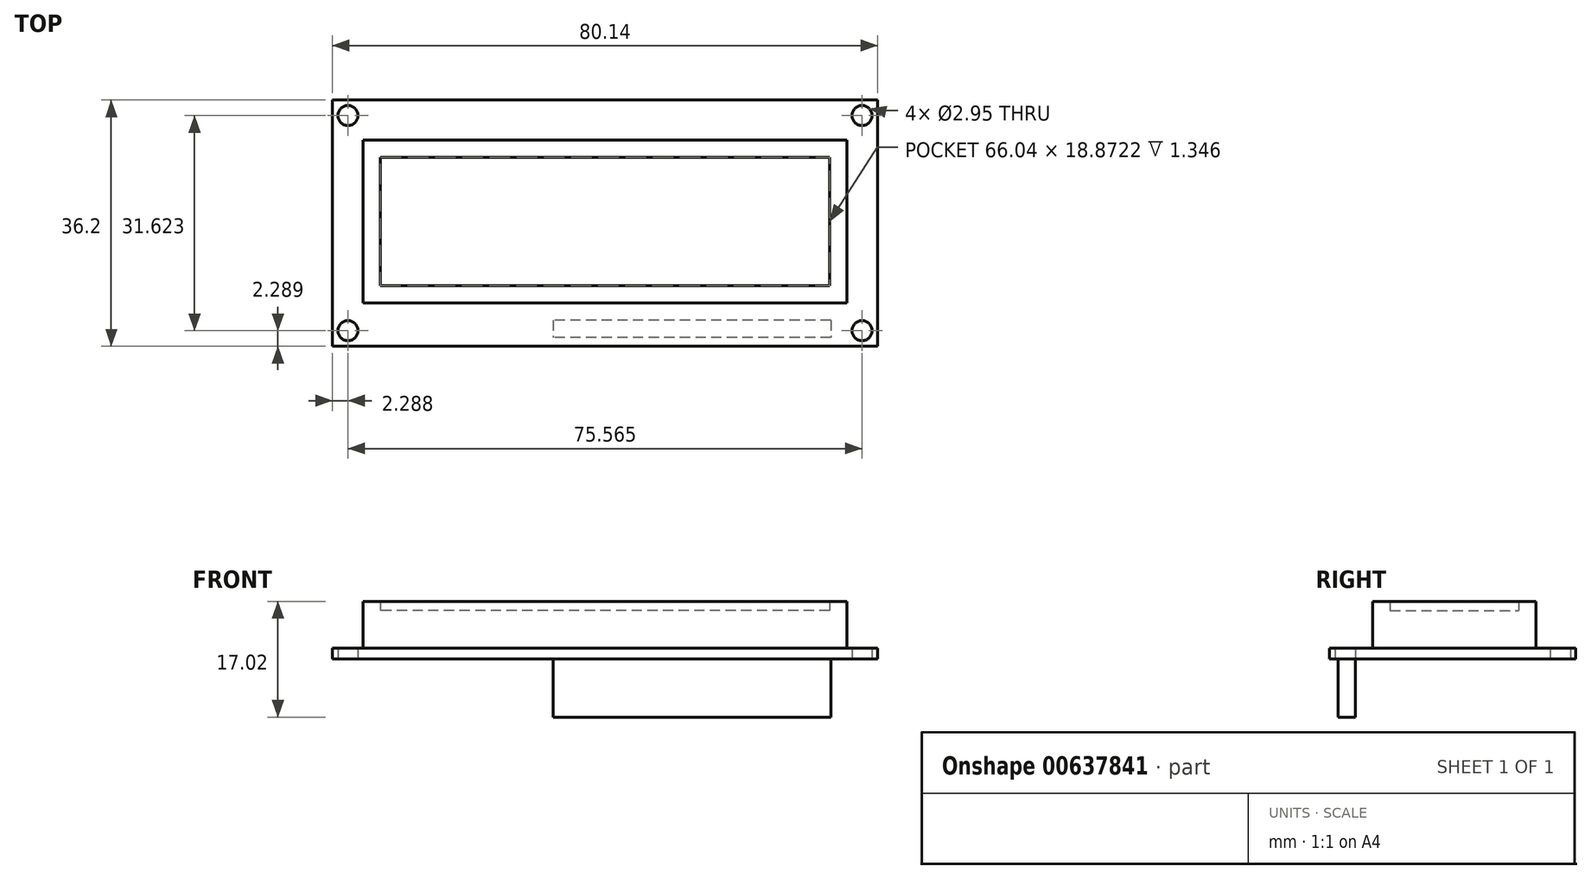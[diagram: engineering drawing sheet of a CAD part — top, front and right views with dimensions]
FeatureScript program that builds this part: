
annotation { "Feature Type Name" : "Feature", "Feature Type Description" : "" }
export const myFeature = defineFeature(function(context is Context, id is Id, definition is map)
    precondition{}
    {
        {
            var Q0;
            Q0=qCreatedBy(makeId("Top.planeOp"),FACE);
            var sketch = newSketch(context, id + "F0", { "sketchPlane" : qUnion([Q0])});
            skLineSegment(sketch, "E0.bottom", {"start": v(40.07, -18.1) * mm, "end": v(-40.07, -18.1) * mm});
            skLineSegment(sketch, "E0.top", {"start": v(40.07, 18.1) * mm, "end": v(-40.07, 18.1) * mm});
            skLineSegment(sketch, "E0.left", {"start": v(40.07, -18.1) * mm, "end": v(40.07, 18.1) * mm});
            skLineSegment(sketch, "E0.right", {"start": v(-40.07, -18.1) * mm, "end": v(-40.07, 18.1) * mm});
            skPoint(sketch, "E0.middle", {"position": v(0, 0) * mm});
            skCircle(sketch, "E1", {"center": v(-37.78, 15.81) * mm, "radius": 1.47 * mm});
            skCircle(sketch, "E2", {"center": v(37.78, 15.81) * mm, "radius": 1.47 * mm});
            skCircle(sketch, "E3", {"center": v(37.78, -15.81) * mm, "radius": 1.47 * mm});
            skCircle(sketch, "E4", {"center": v(-37.78, -15.81) * mm, "radius": 1.47 * mm});
            skSolve(sketch);
        }
        {
            var Q0;
            Q0=makeQuery(id+"F0.imprint","IMPRINT",FACE,{"disambiguationData":[TD([[makeQuery(id+"F0.imprint","IMPRINT",EDGE,{"derivedFrom":sQuery(id+"F0.wireOp",EDGE,"E0.bottom")}),-1.0]])]});
            extrude(context, id + "F1", {"entities" : qUnion([Q0]), "depth" : 1.6 * mm, "offsetDistance" : 25.4 * mm});
        }
        {
            var Q0;
            Q0=makeQuery(id+"F1.opExtrude","CAP_FACE",FACE,{"disambiguationData":[OSD([sQuery(id+"F0.wireOp",EDGE,"E0.bottom"),sQuery(id+"F0.wireOp",EDGE,"E0.top"),sQuery(id+"F0.wireOp",EDGE,"E0.left"),sQuery(id+"F0.wireOp",EDGE,"E0.right"),sQuery(id+"F0.wireOp",EDGE,"E1"),sQuery(id+"F0.wireOp",EDGE,"E2"),sQuery(id+"F0.wireOp",EDGE,"E3"),sQuery(id+"F0.wireOp",EDGE,"E4")])],"isStart":false});
            var sketch = newSketch(context, id + "F2", { "sketchPlane" : qUnion([Q0])});
            skLineSegment(sketch, "E5.bottom", {"start": v(-35.56, 12.2) * mm, "end": v(35.56, 12.2) * mm});
            skLineSegment(sketch, "E5.top", {"start": v(-35.56, -11.75) * mm, "end": v(35.56, -11.75) * mm});
            skLineSegment(sketch, "E5.left", {"start": v(-35.56, 12.2) * mm, "end": v(-35.56, -11.75) * mm});
            skLineSegment(sketch, "E5.right", {"start": v(35.56, 12.2) * mm, "end": v(35.56, -11.75) * mm});
            skLineSegment(sketch, "E6", {"start": v(0, 18.1) * mm, "end": v(0, -18.1) * mm, "construction": true});
            skLineSegment(sketch, "E7", {"start": v(0, 12.2) * mm, "end": v(0, -11.75) * mm, "construction": true});
            skSolve(sketch);
        }
        {
            var Q0;
            Q0=makeQuery(id+"F2.imprint","IMPRINT",FACE,{"disambiguationData":[TD([[makeQuery(id+"F2.imprint","IMPRINT",EDGE,{"derivedFrom":sQuery(id+"F2.wireOp",EDGE,"E5.bottom")}),-1.0]])]});
            extrude(context, id + "F3", {"entities" : qUnion([Q0]), "operationType" : NewBodyOperationType.ADD, "depth" : 6.86 * mm, "offsetDistance" : 25.4 * mm});
        }
        {
            var Q0;
            Q0=makeQuery(id+"F3.opExtrude","CAP_FACE",FACE,{"disambiguationData":[OSD([sQuery(id+"F2.wireOp",EDGE,"E5.bottom"),sQuery(id+"F2.wireOp",EDGE,"E5.top"),sQuery(id+"F2.wireOp",EDGE,"E5.left"),sQuery(id+"F2.wireOp",EDGE,"E5.right")])],"isStart":false});
            shell(context, id + "F4", {"entities" : qUnion([Q0]), "thickness" : 2.54 * mm});
        }
        {
            var Q0;
            Q0=makeQuery(id+"F4.opShell","OFFSET_FACE",FACE,{"disambiguationData":[OSD([sQuery(id+"F0.wireOp",EDGE,"E0.bottom"),sQuery(id+"F0.wireOp",EDGE,"E0.top"),sQuery(id+"F0.wireOp",EDGE,"E0.left"),sQuery(id+"F0.wireOp",EDGE,"E0.right"),sQuery(id+"F0.wireOp",EDGE,"E1"),sQuery(id+"F0.wireOp",EDGE,"E2"),sQuery(id+"F0.wireOp",EDGE,"E3"),sQuery(id+"F0.wireOp",EDGE,"E4")])]});
            extrude(context, id + "F5", {"entities" : qUnion([Q0]), "operationType" : NewBodyOperationType.ADD, "depth" : 4.57 * mm, "offsetDistance" : 25.4 * mm});
        }
        {
            var Q0;
            Q0=makeQuery(id+"F1.opExtrude","CAP_FACE",FACE,{"disambiguationData":[OSD([sQuery(id+"F0.wireOp",EDGE,"E0.bottom"),sQuery(id+"F0.wireOp",EDGE,"E0.top"),sQuery(id+"F0.wireOp",EDGE,"E0.left"),sQuery(id+"F0.wireOp",EDGE,"E0.right"),sQuery(id+"F0.wireOp",EDGE,"E1"),sQuery(id+"F0.wireOp",EDGE,"E2"),sQuery(id+"F0.wireOp",EDGE,"E3"),sQuery(id+"F0.wireOp",EDGE,"E4")])],"isStart":true});
            var sketch = newSketch(context, id + "F6", { "sketchPlane" : qUnion([Q0])});
            skLineSegment(sketch, "E8.bottom", {"start": v(33.21, 14.29) * mm, "end": v(-7.63, 14.29) * mm});
            skLineSegment(sketch, "E8.top", {"start": v(33.21, 16.83) * mm, "end": v(-7.63, 16.83) * mm});
            skLineSegment(sketch, "E8.left", {"start": v(33.21, 14.29) * mm, "end": v(33.21, 16.83) * mm});
            skLineSegment(sketch, "E8.right", {"start": v(-7.63, 14.29) * mm, "end": v(-7.63, 16.83) * mm});
            skSolve(sketch);
        }
        {
            var Q0;
            Q0=makeQuery(id+"F6.imprint","IMPRINT",FACE,{"disambiguationData":[TD([[makeQuery(id+"F6.imprint","IMPRINT",EDGE,{"derivedFrom":sQuery(id+"F6.wireOp",EDGE,"E8.bottom")}),-1.0]])]});
            var Q1;
            Q1 = qSketchRegion(id + "F6", true);
            extrude(context, id + "F7", {"entities" : qUnion([Q0, Q1]), "operationType" : NewBodyOperationType.ADD, "depth" : 8.56 * mm, "offsetDistance" : 25.4 * mm});
        }
    });
